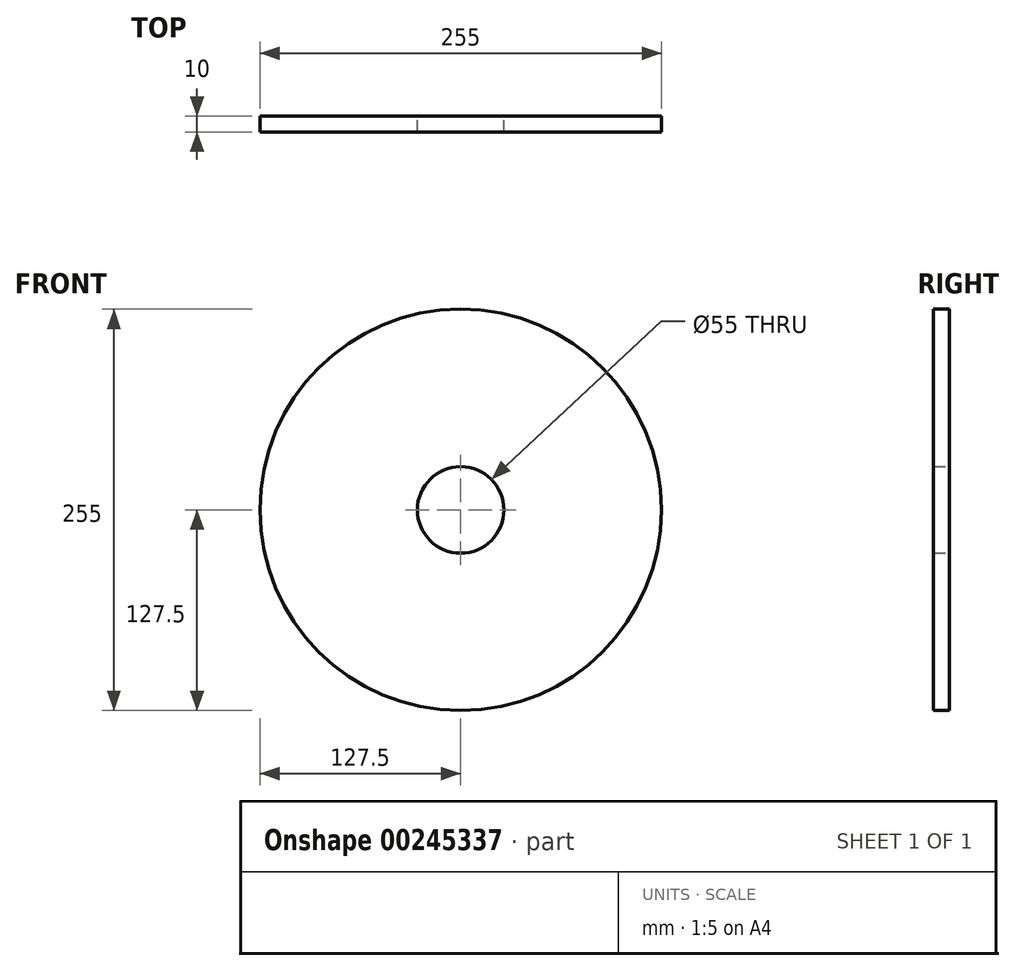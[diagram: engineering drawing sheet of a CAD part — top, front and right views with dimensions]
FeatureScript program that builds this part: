
annotation { "Feature Type Name" : "Feature", "Feature Type Description" : "" }
export const myFeature = defineFeature(function(context is Context, id is Id, definition is map)
    precondition{}
    {
        {
            var Q0;
            Q0=qCreatedBy(makeId("Front.planeOp"),FACE);
            var sketch = newSketch(context, id + "F0", { "sketchPlane" : qUnion([Q0])});
            skCircle(sketch, "E0", {"center": v(0, 0) * mm, "radius": 27.5 * mm});
            skCircle(sketch, "E1", {"center": v(0, 0) * mm, "radius": 127.5 * mm});
            skSolve(sketch);
        }
        {
            var Q0;
            Q0=makeQuery(id+"F0.imprint","IMPRINT",FACE,{"disambiguationData":[TD([[makeQuery(id+"F0.imprint","IMPRINT",EDGE,{"derivedFrom":sQuery(id+"F0.wireOp",EDGE,"E0")}),-1.0]])]});
            extrude(context, id + "F1", {"entities" : qUnion([Q0]), "depth" : 10 * mm});
        }
    });
